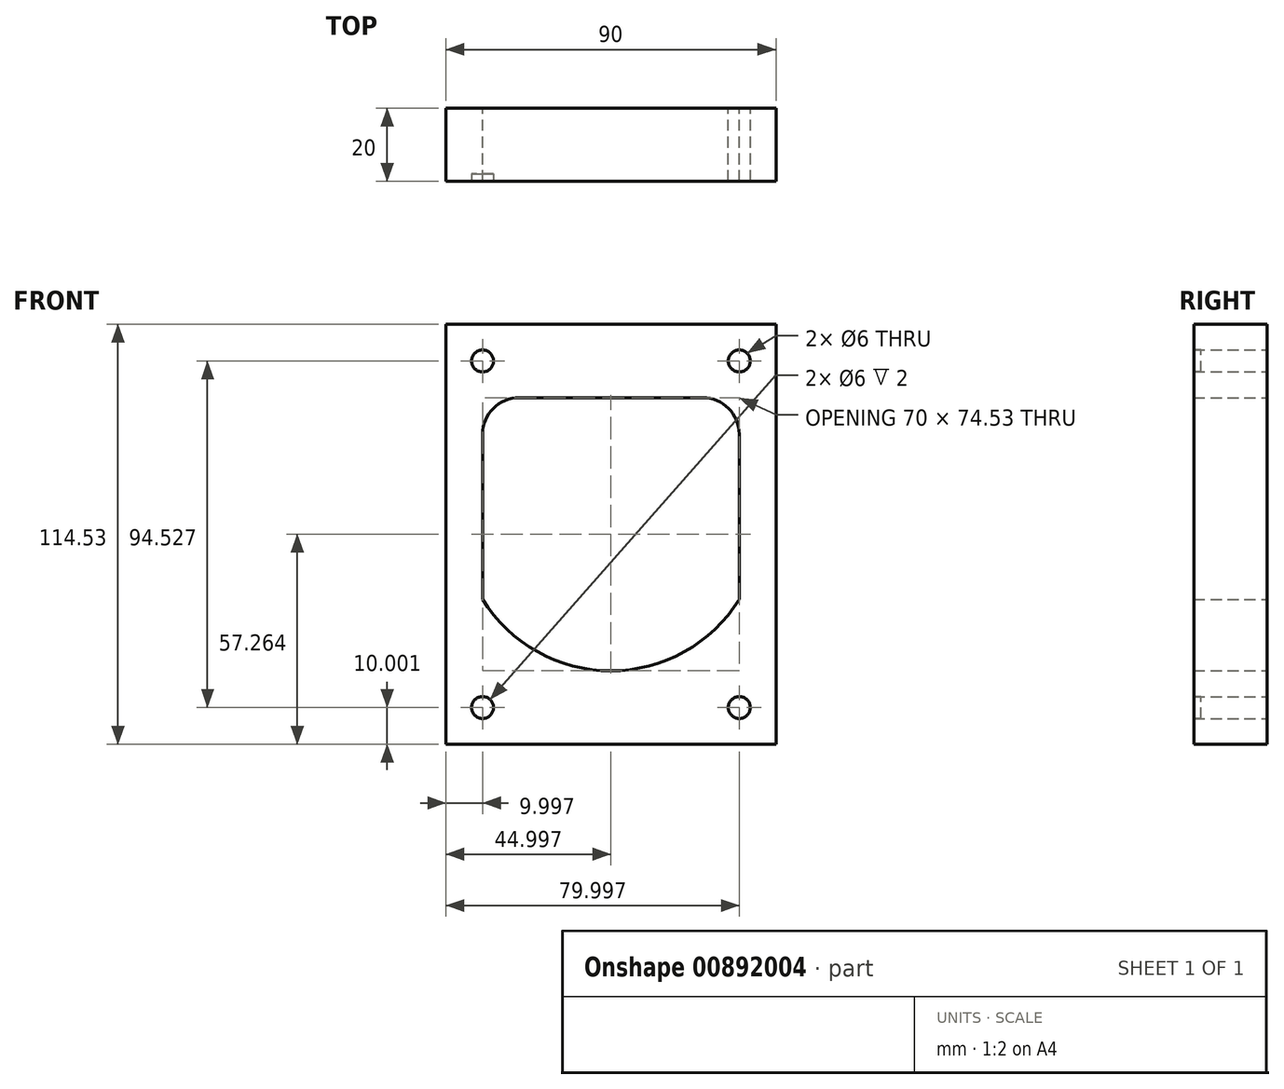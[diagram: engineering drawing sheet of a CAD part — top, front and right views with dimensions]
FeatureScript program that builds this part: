
annotation { "Feature Type Name" : "Feature", "Feature Type Description" : "" }
export const myFeature = defineFeature(function(context is Context, id is Id, definition is map)
    precondition{}
    {
        {
            var Q0;
            Q0=qCreatedBy(makeId("Front.planeOp"),FACE);
            var sketch = newSketch(context, id + "F0", { "sketchPlane" : qUnion([Q0])});
            skLineSegment(sketch, "E0.bottom", {"start": v(-14.68, 26.24) * mm, "end": v(35.32, 26.24) * mm});
            skLineSegment(sketch, "E0.left", {"start": v(-24.68, 16.24) * mm, "end": v(-24.68, -28.76) * mm});
            skLineSegment(sketch, "E0.right", {"start": v(45.32, 16.24) * mm, "end": v(45.32, -28.76) * mm});
            skLineSegment(sketch, "E1", {"start": v(10.32, -48.29) * mm, "end": v(10.32, 26.24) * mm, "construction": true});
            skLineSegment(sketch, "E2", {"start": v(-24.68, -28.76) * mm, "end": v(45.32, -28.76) * mm, "construction": true});
            skPoint(sketch, "E3.orphan", {"position": v(45.32, -48.29) * mm});
            skPoint(sketch, "E4.orphan", {"position": v(-24.68, -48.29) * mm});
            skArc(sketch, "E5", {"start": v(-24.68, -28.76) * mm, "mid": v(10.32, -48.29) * mm, "end": v(45.32, -28.76) * mm});
            skPoint(sketch, "E6.visualSharp", {"position": v(-24.68, 26.24) * mm});
            skArc(sketch, "E6.filletArc", {"start": v(-14.68, 26.24) * mm, "mid": v(-21.75, 23.3) * mm, "end": v(-24.68, 16.24) * mm});
            skPoint(sketch, "E7.visualSharp", {"position": v(45.32, 26.24) * mm});
            skArc(sketch, "E7.filletArc", {"start": v(45.32, 16.24) * mm, "mid": v(42.39, 23.3) * mm, "end": v(35.32, 26.24) * mm});
            skLineSegment(sketch, "E8.bottom", {"start": v(-34.68, 46.24) * mm, "end": v(55.32, 46.24) * mm});
            skLineSegment(sketch, "E8.top", {"start": v(-34.68, -68.29) * mm, "end": v(55.32, -68.29) * mm});
            skLineSegment(sketch, "E8.left", {"start": v(-34.68, 46.24) * mm, "end": v(-34.68, -68.29) * mm});
            skLineSegment(sketch, "E8.right", {"start": v(55.32, 46.24) * mm, "end": v(55.32, -68.29) * mm});
            skCircle(sketch, "E9", {"center": v(-24.68, -58.29) * mm, "radius": 3 * mm});
            skCircle(sketch, "E10.MirrorC", {"center": v(45.32, -58.29) * mm, "radius": 3 * mm});
            skCircle(sketch, "E11", {"center": v(-24.68, 36.24) * mm, "radius": 3 * mm});
            skCircle(sketch, "E12.MirrorC", {"center": v(45.32, 36.24) * mm, "radius": 3 * mm});
            skSolve(sketch);
        }
        {
            var Q0;
            Q0=makeQuery(id+"F0.imprint","IMPRINT",FACE,{"disambiguationData":[TD([[makeQuery(id+"F0.imprint","IMPRINT",EDGE,{"derivedFrom":sQuery(id+"F0.wireOp",EDGE,"E0.bottom")}),1.0]])]});
            var Q1;
            Q1=makeQuery(id+"F0.imprint","IMPRINT",FACE,{"disambiguationData":[TD([[makeQuery(id+"F0.imprint","IMPRINT",EDGE,{"derivedFrom":sQuery(id+"F0.wireOp",EDGE,"E10.MirrorC")}),-1.0]])]});
            var Q2;
            Q2=makeQuery(id+"F0.imprint","IMPRINT",FACE,{"disambiguationData":[TD([[makeQuery(id+"F0.imprint","IMPRINT",EDGE,{"derivedFrom":sQuery(id+"F0.wireOp",EDGE,"E9")}),1.0]])]});
            var Q3;
            Q3=makeQuery(id+"F0.imprint","IMPRINT",FACE,{"disambiguationData":[TD([[makeQuery(id+"F0.imprint","IMPRINT",EDGE,{"derivedFrom":sQuery(id+"F0.wireOp",EDGE,"E12.MirrorC")}),-1.0]])]});
            var Q4;
            Q4=makeQuery(id+"F0.imprint","IMPRINT",FACE,{"disambiguationData":[TD([[makeQuery(id+"F0.imprint","IMPRINT",EDGE,{"derivedFrom":sQuery(id+"F0.wireOp",EDGE,"E11")}),1.0]])]});
            extrude(context, id + "F1", {"entities" : qUnion([Q0, Q1, Q2, Q3, Q4]), "depth" : 20 * mm, "offsetDistance" : 25 * mm});
        }
        {
            var Q0;
            Q0=makeQuery(id+"F1.opExtrude","CAP_FACE",FACE,{"disambiguationData":[OSD([sQuery(id+"F0.wireOp",EDGE,"E0.bottom"),sQuery(id+"F0.wireOp",EDGE,"E0.left"),sQuery(id+"F0.wireOp",EDGE,"E0.right"),sQuery(id+"F0.wireOp",EDGE,"E5"),sQuery(id+"F0.wireOp",EDGE,"E6.filletArc"),sQuery(id+"F0.wireOp",EDGE,"E7.filletArc"),sQuery(id+"F0.wireOp",EDGE,"E8.bottom"),sQuery(id+"F0.wireOp",EDGE,"E8.top"),sQuery(id+"F0.wireOp",EDGE,"E8.left"),sQuery(id+"F0.wireOp",EDGE,"E8.right")])],"isStart":false});
            var sketch = newSketch(context, id + "F2", { "sketchPlane" : qUnion([Q0])});
            skCircle(sketch, "E13", {"center": v(-24.68, 36.24) * mm, "radius": 3 * mm});
            skLineSegment(sketch, "E14", {"start": v(10.32, 46.24) * mm, "end": v(10.32, -68.29) * mm, "construction": true});
            skLineSegment(sketch, "E15", {"start": v(-34.68, -11.03) * mm, "end": v(55.32, -11.03) * mm, "construction": true});
            skCircle(sketch, "E16.MirrorC", {"center": v(45.32, 36.24) * mm, "radius": 3 * mm});
            skCircle(sketch, "E17.MirrorC", {"center": v(-24.68, -58.29) * mm, "radius": 3 * mm});
            skCircle(sketch, "E18.MirrorC", {"center": v(45.32, -58.29) * mm, "radius": 3 * mm});
            skSolve(sketch);
        }
        {
            var Q0;
            Q0 = qSketchRegion(id + "F2", true);
            extrude(context, id + "F3", {"entities" : qUnion([Q0]), "operationType" : NewBodyOperationType.REMOVE, "oppositeDirection" : true, "depth" : 2 * mm, "offsetDistance" : 25 * mm});
        }
    });
